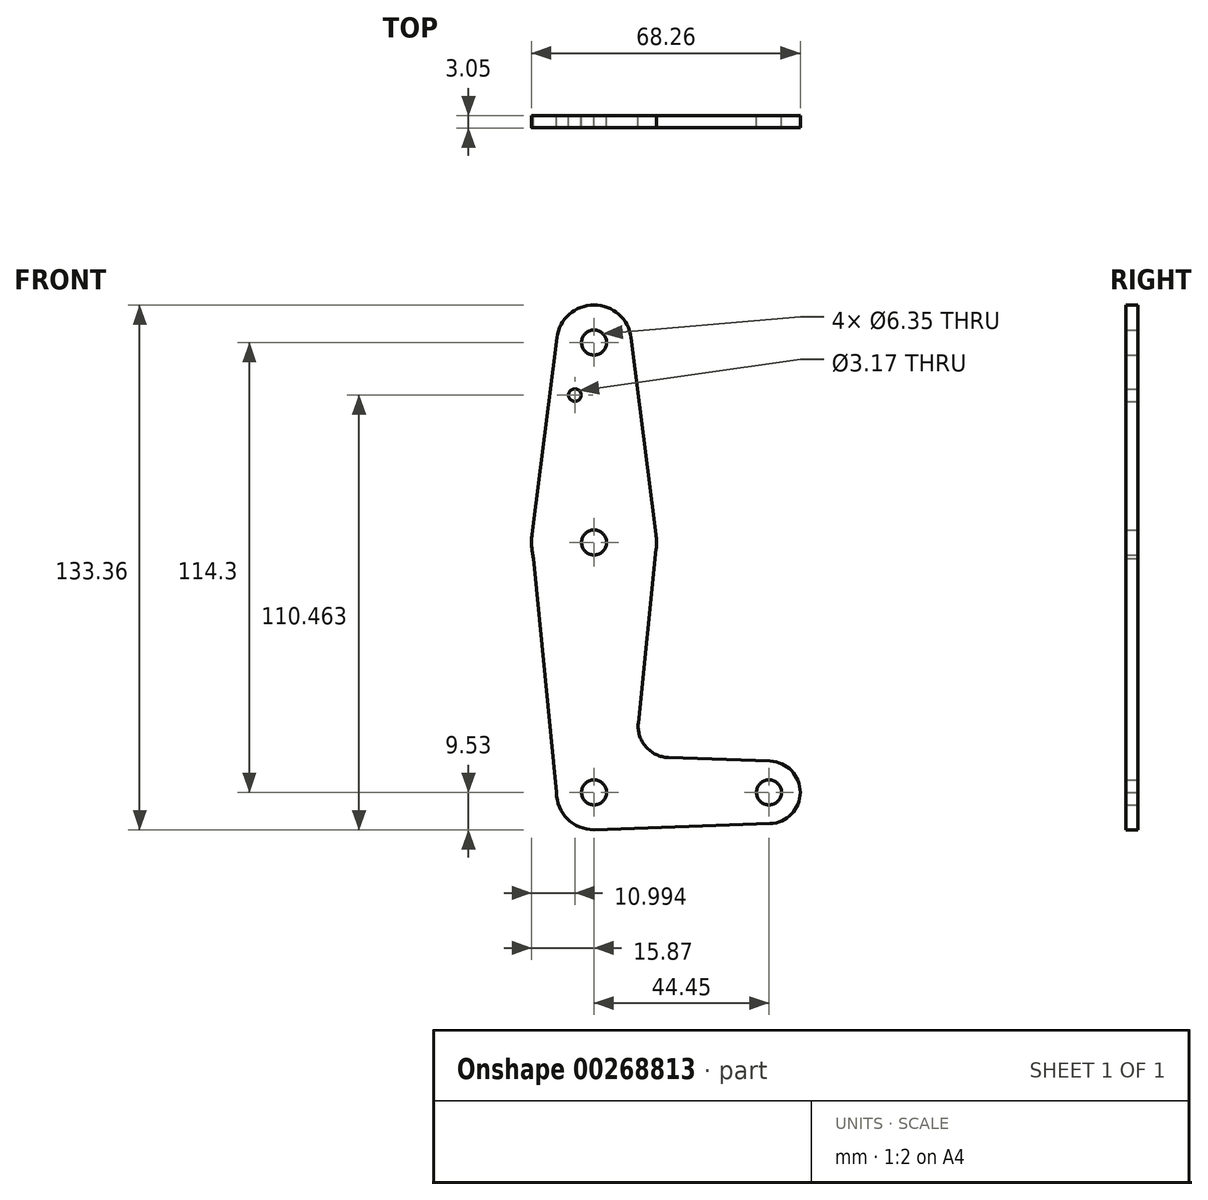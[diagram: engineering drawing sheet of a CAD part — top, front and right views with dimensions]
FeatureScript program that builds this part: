
annotation { "Feature Type Name" : "Feature", "Feature Type Description" : "" }
export const myFeature = defineFeature(function(context is Context, id is Id, definition is map)
    precondition{}
    {
        {
            var Q0;
            Q0=qCreatedBy(makeId("Front.planeOp"),FACE);
            var sketch = newSketch(context, id + "F0", { "sketchPlane" : qUnion([Q0])});
            skLineSegment(sketch, "E0", {"start": v(44.45, 0) * mm, "end": v(0, 0) * mm, "construction": true});
            skLineSegment(sketch, "E1", {"start": v(0, 0) * mm, "end": v(0, 63.5) * mm, "construction": true});
            skLineSegment(sketch, "E2", {"start": v(0, 63.5) * mm, "end": v(0, 114.3) * mm, "construction": true});
            skCircle(sketch, "E3", {"center": v(44.45, 0) * mm, "radius": 7.94 * mm});
            skCircle(sketch, "E4", {"center": v(0, 0) * mm, "radius": 9.53 * mm});
            skCircle(sketch, "E5", {"center": v(0, 63.5) * mm, "radius": 15.88 * mm});
            skCircle(sketch, "E6", {"center": v(0, 114.3) * mm, "radius": 9.53 * mm});
            skLineSegment(sketch, "E7", {"start": v(-9.45, 115.5) * mm, "end": v(-15.75, 65.48) * mm});
            skLineSegment(sketch, "E8", {"start": v(9.45, 115.5) * mm, "end": v(15.75, 65.48) * mm});
            skLineSegment(sketch, "E9", {"start": v(-9.53, 0) * mm, "end": v(-15.75, 63.5) * mm});
            skLineSegment(sketch, "E10", {"start": v(11.25, 17.6) * mm, "end": v(15.96, 63.5) * mm});
            skPoint(sketch, "E10.startSnap0", {"position": v(22.23, 0) * mm});
            skLineSegment(sketch, "E11", {"start": v(0, -9.53) * mm, "end": v(44.73, -7.93) * mm});
            skLineSegment(sketch, "E12", {"start": v(44.73, 7.93) * mm, "end": v(18.88, 8.85) * mm});
            skCircle(sketch, "E13", {"center": v(0, 114.3) * mm, "radius": 3.18 * mm});
            skCircle(sketch, "E14", {"center": v(0, 63.5) * mm, "radius": 3.18 * mm});
            skCircle(sketch, "E15", {"center": v(0, 0) * mm, "radius": 3.18 * mm});
            skCircle(sketch, "E16", {"center": v(44.45, 0) * mm, "radius": 3.18 * mm});
            skCircle(sketch, "E17", {"center": v(-4.88, 100.93) * mm, "radius": 1.59 * mm});
            skPoint(sketch, "E18.newPointA", {"position": v(9.45, 0) * mm});
            skArc(sketch, "E18.filletArc", {"start": v(11.25, 17.6) * mm, "mid": v(13.17, 11.58) * mm, "end": v(18.88, 8.85) * mm});
            skSolve(sketch);
        }
        {
            var Q0;
            Q0=makeQuery(id+"F0.imprint","IMPRINT",FACE,{"disambiguationData":[TD([[makeQuery(id+"F0.imprint","IMPRINT",EDGE,{"derivedFrom":sQuery(id+"F0.wireOp",EDGE,"E13")}),-1.0]])]});
            var Q1;
            {var subQ1=sQuery(id+"F0.wireOp",EDGE,"E7");Q1=makeQuery(id+"F0.imprint","IMPRINT",FACE,{"disambiguationData":[TD([[makeQuery(id+"F0.imprint","IMPRINT",EDGE,{"derivedFrom":subQ1}),1.0]])]});}
            var Q2;
            Q2=makeQuery(id+"F0.imprint","IMPRINT",FACE,{"disambiguationData":[TD([[makeQuery(id+"F0.imprint","IMPRINT",EDGE,{"derivedFrom":sQuery(id+"F0.wireOp",EDGE,"E14")}),-1.0]])]});
            var Q3;
            {var subQ5=sQuery(id+"F0.wireOp",EDGE,"E12");Q3=makeQuery(id+"F0.imprint","IMPRINT",FACE,{"disambiguationData":[TD([[makeQuery(id+"F0.imprint","IMPRINT",EDGE,{"derivedFrom":subQ5}),1.0]])]});}
            var Q4;
            Q4=makeQuery(id+"F0.imprint","IMPRINT",FACE,{"disambiguationData":[TD([[makeQuery(id+"F0.imprint","IMPRINT",EDGE,{"derivedFrom":sQuery(id+"F0.wireOp",EDGE,"E15")}),-1.0]])]});
            var Q5;
            Q5=makeQuery(id+"F0.imprint","IMPRINT",FACE,{"disambiguationData":[TD([[makeQuery(id+"F0.imprint","IMPRINT",EDGE,{"derivedFrom":sQuery(id+"F0.wireOp",EDGE,"E16")}),-1.0]])]});
            extrude(context, id + "F1", {"entities" : qUnion([Q0, Q1, Q2, Q3, Q4, Q5]), "depth" : 3.05 * mm});
        }
    });
